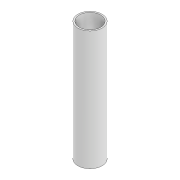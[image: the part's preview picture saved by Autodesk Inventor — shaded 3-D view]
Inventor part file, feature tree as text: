
AUTODESK INVENTOR PART (.ipt)
format: ipt  version: 2022.3 (Build 263350000, 350)  size: 82,944 bytes
history: native  units: mm
features: other x1, extrude x1, sketch x1
ambient origin geometry x8: Origin, YZ Plane, XZ Plane, XY Plane, X Axis, Y Axis, Z Axis, Center Point
bodies: Body1 (feature_tree)
feature tree (3):
  other  "Sólido1"
  extrude  "Extrusión1"  Depth=245.0mm
  sketch  "Boceto1"  dims[d0=49.75mm d1=43.9mm d2=245.0mm d3=0.0mm]
